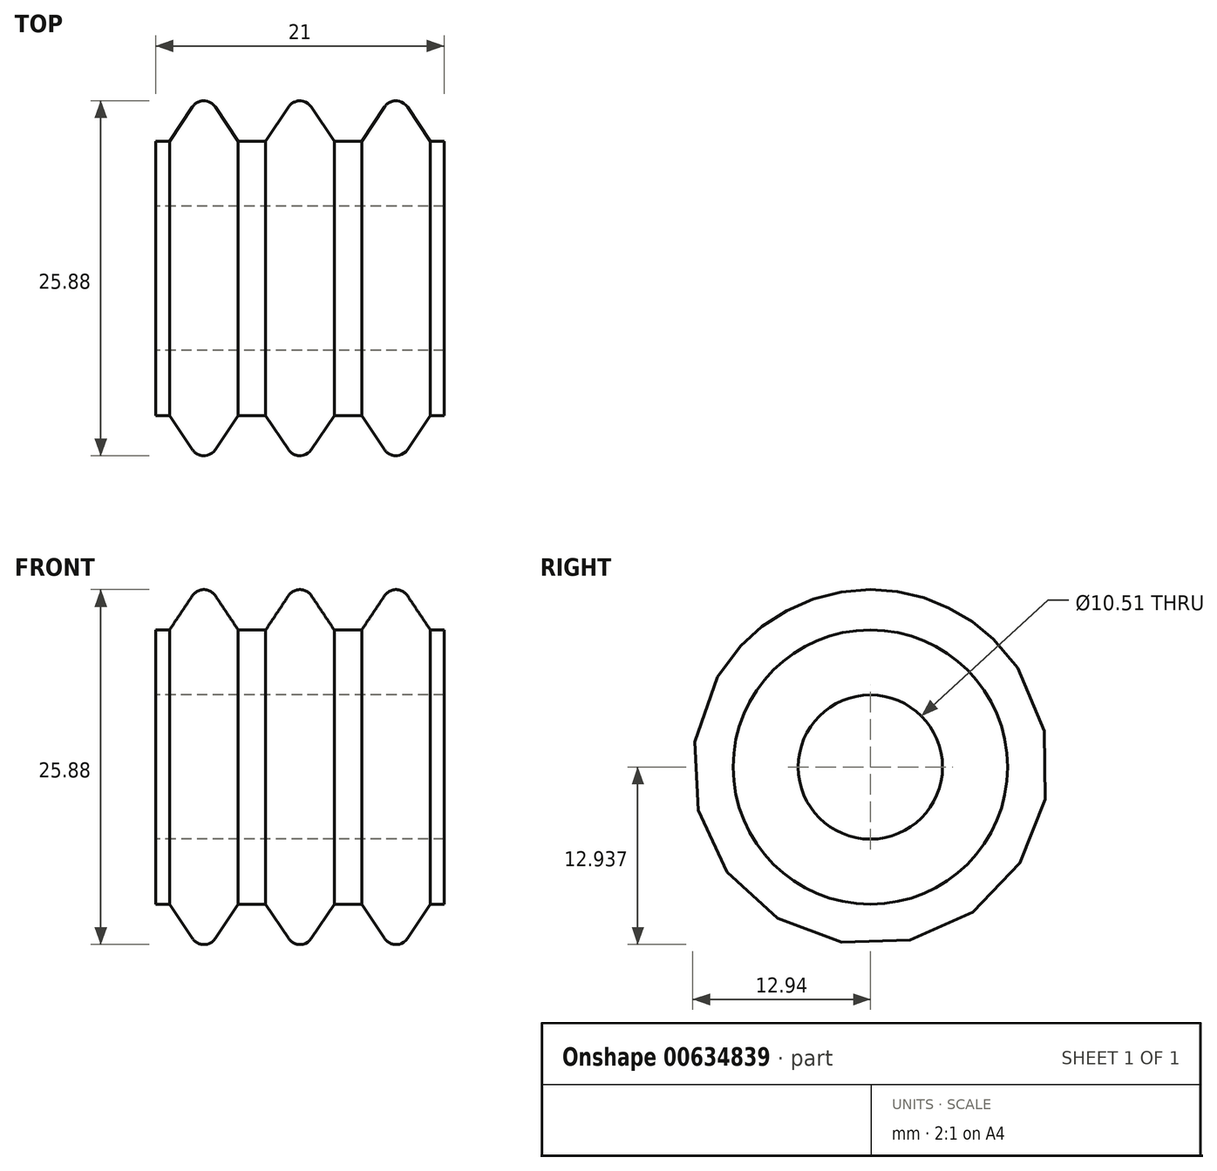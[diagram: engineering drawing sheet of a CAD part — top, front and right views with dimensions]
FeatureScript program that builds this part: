
annotation { "Feature Type Name" : "Feature", "Feature Type Description" : "" }
export const myFeature = defineFeature(function(context is Context, id is Id, definition is map)
    precondition{}
    {
        {
            var Q0;
            Q0=qCreatedBy(makeId("Front.planeOp"),FACE);
            var sketch = newSketch(context, id + "F0", { "sketchPlane" : qUnion([Q0])});
            skLineSegment(sketch, "E0", {"start": v(-10.5, 25.6) * mm, "end": v(10.5, 25.6) * mm});
            skLineSegment(sketch, "E1", {"start": v(10.5, 25.6) * mm, "end": v(10.5, 35.6) * mm});
            skLineSegment(sketch, "E2", {"start": v(10.5, 35.6) * mm, "end": v(9.5, 35.6) * mm});
            skLineSegment(sketch, "E3", {"start": v(9.5, 35.6) * mm, "end": v(7.83, 38.1) * mm});
            skLineSegment(sketch, "E4", {"start": v(6.17, 38.1) * mm, "end": v(4.5, 35.6) * mm});
            skLineSegment(sketch, "E5", {"start": v(4.5, 35.6) * mm, "end": v(2.5, 35.6) * mm});
            skLineSegment(sketch, "E6", {"start": v(2.5, 35.6) * mm, "end": v(0.83, 38.1) * mm});
            skLineSegment(sketch, "E7", {"start": v(-0.83, 38.1) * mm, "end": v(-2.5, 35.6) * mm});
            skLineSegment(sketch, "E8", {"start": v(-2.5, 35.6) * mm, "end": v(-4.5, 35.6) * mm});
            skLineSegment(sketch, "E9", {"start": v(-4.5, 35.6) * mm, "end": v(-6.17, 38.1) * mm});
            skLineSegment(sketch, "E10", {"start": v(-7.83, 38.1) * mm, "end": v(-9.5, 35.6) * mm});
            skLineSegment(sketch, "E11", {"start": v(-9.5, 35.6) * mm, "end": v(-10.5, 35.6) * mm});
            skLineSegment(sketch, "E12", {"start": v(-10.5, 35.6) * mm, "end": v(-10.5, 25.6) * mm});
            skPoint(sketch, "E13.visualSharp", {"position": v(-7, 39.34) * mm});
            skArc(sketch, "E13.filletArc", {"start": v(-6.17, 38.1) * mm, "mid": v(-7, 38.54) * mm, "end": v(-7.83, 38.1) * mm});
            skPoint(sketch, "E14.visualSharp", {"position": v(0, 39.34) * mm});
            skArc(sketch, "E14.filletArc", {"start": v(0.83, 38.1) * mm, "mid": v(0, 38.54) * mm, "end": v(-0.83, 38.1) * mm});
            skPoint(sketch, "E15.visualSharp", {"position": v(7, 39.34) * mm});
            skArc(sketch, "E15.filletArc", {"start": v(7.83, 38.1) * mm, "mid": v(7, 38.54) * mm, "end": v(6.17, 38.1) * mm});
            skSolve(sketch);
        }
        {
            var Q0;
            Q0=makeQuery(id+"F0.imprint","IMPRINT",FACE,{"disambiguationData":[TD([[makeQuery(id+"F0.imprint","IMPRINT",EDGE,{"derivedFrom":sQuery(id+"F0.wireOp",EDGE,"E0")}),1.0]])]});
            var Q1;
            Q1=sQuery(id+"F0.wireOp",EDGE,"E0");
            revolve(context, id + "F1", {"entities" : qUnion([Q0]), "axis" : qUnion([Q1]), "revolveType" : RevolveType.FULL});
        }
        {
            var Q0;
            Q0=makeQuery(id+"F1.opRevolve","SWEPT_FACE",FACE,{"disambiguationData":[OSD([sQuery(id+"F0.wireOp",EDGE,"E12")])]});
            var sketch = newSketch(context, id + "F2", { "sketchPlane" : qUnion([Q0])});
            skCircle(sketch, "E16", {"center": v(0, 25.6) * mm, "radius": 5.25 * mm});
            skSolve(sketch);
        }
        {
            var Q0;
            Q0=makeQuery(id+"F2.imprint","IMPRINT",FACE,{"disambiguationData":[TD([[makeQuery(id+"F2.imprint","IMPRINT",EDGE,{"derivedFrom":sQuery(id+"F2.wireOp",EDGE,"E16")}),1.0]])]});
            extrude(context, id + "F3", {"entities" : qUnion([Q0]), "operationType" : NewBodyOperationType.REMOVE, "endBound" : BoundingType.THROUGH_ALL, "oppositeDirection" : true, "depth" : 25 * mm, "offsetDistance" : 25 * mm});
        }
    });
